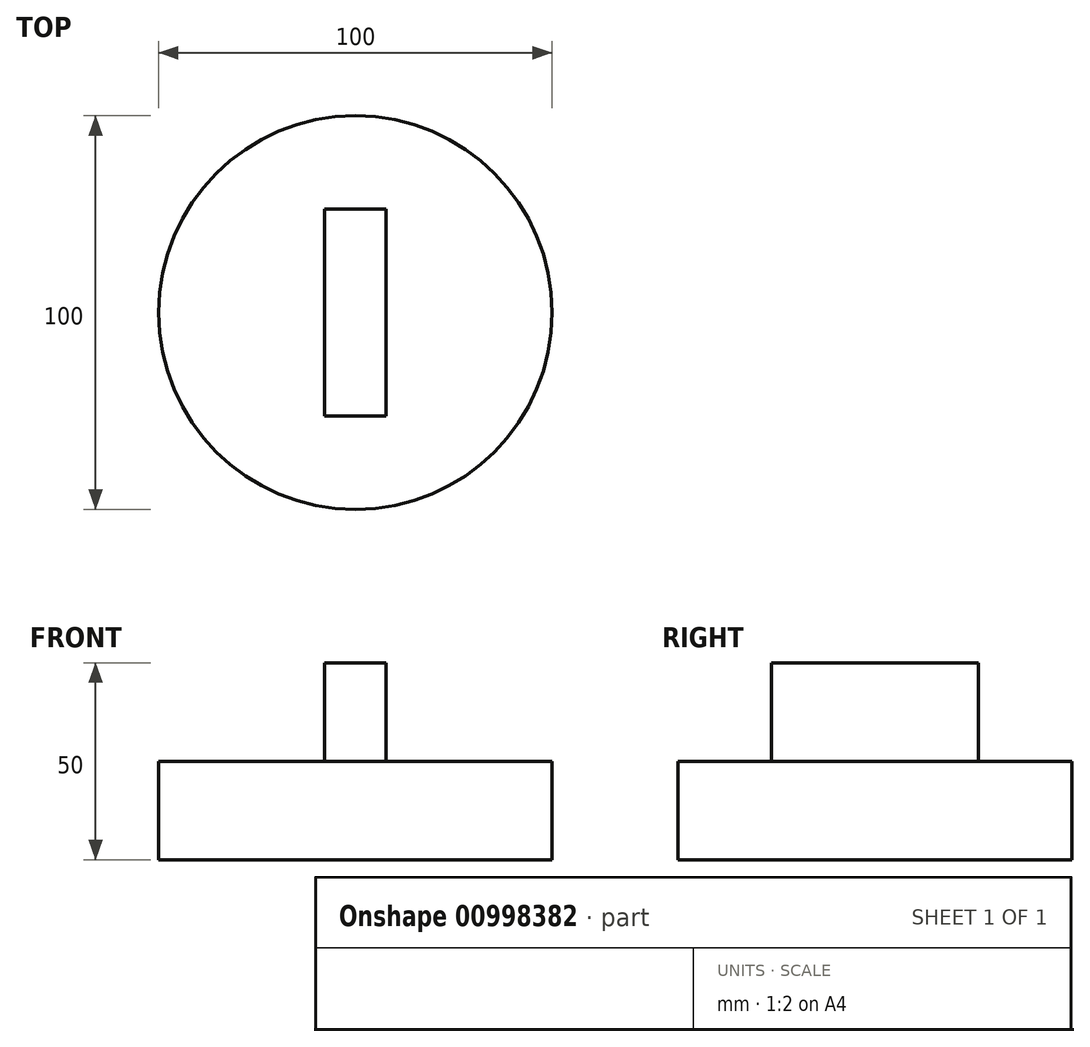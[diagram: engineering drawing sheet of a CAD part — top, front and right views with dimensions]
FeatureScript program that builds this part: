
annotation { "Feature Type Name" : "Feature", "Feature Type Description" : "" }
export const myFeature = defineFeature(function(context is Context, id is Id, definition is map)
    precondition{}
    {
        {
            var Q0;
            Q0=qCreatedBy(makeId("Top.planeOp"),FACE);
            var sketch = newSketch(context, id + "F0", { "sketchPlane" : qUnion([Q0])});
            skCircle(sketch, "E0", {"center": v(0, 0) * mm, "radius": 50 * mm});
            skSolve(sketch);
        }
        {
            var Q0;
            Q0=makeQuery(id+"F0.imprint","IMPRINT",FACE,{"disambiguationData":[TD([[makeQuery(id+"F0.imprint","IMPRINT",EDGE,{"derivedFrom":sQuery(id+"F0.wireOp",EDGE,"E0")}),1.0]])]});
            extrude(context, id + "F1", {"entities" : qUnion([Q0]), "depth" : 25 * mm, "offsetDistance" : 25 * mm});
        }
        {
            var Q0;
            Q0=makeQuery(id+"F1.opExtrude","CAP_FACE",FACE,{"disambiguationData":[OSD([sQuery(id+"F0.wireOp",EDGE,"E0")])],"isStart":false});
            var sketch = newSketch(context, id + "F2", { "sketchPlane" : qUnion([Q0])});
            skLineSegment(sketch, "E1.bottom", {"start": v(7.82, -26.27) * mm, "end": v(-7.82, -26.27) * mm});
            skLineSegment(sketch, "E1.top", {"start": v(7.82, 26.27) * mm, "end": v(-7.82, 26.27) * mm});
            skLineSegment(sketch, "E1.left", {"start": v(7.82, -26.27) * mm, "end": v(7.82, 26.27) * mm});
            skLineSegment(sketch, "E1.right", {"start": v(-7.82, -26.27) * mm, "end": v(-7.82, 26.27) * mm});
            skPoint(sketch, "E1.middle", {"position": v(0, 0) * mm});
            skSolve(sketch);
        }
        {
            var Q0;
            Q0 = qSketchRegion(id + "F2", true);
            extrude(context, id + "F3", {"entities" : qUnion([Q0]), "operationType" : NewBodyOperationType.ADD, "depth" : 25 * mm, "offsetDistance" : 25 * mm});
        }
    });
